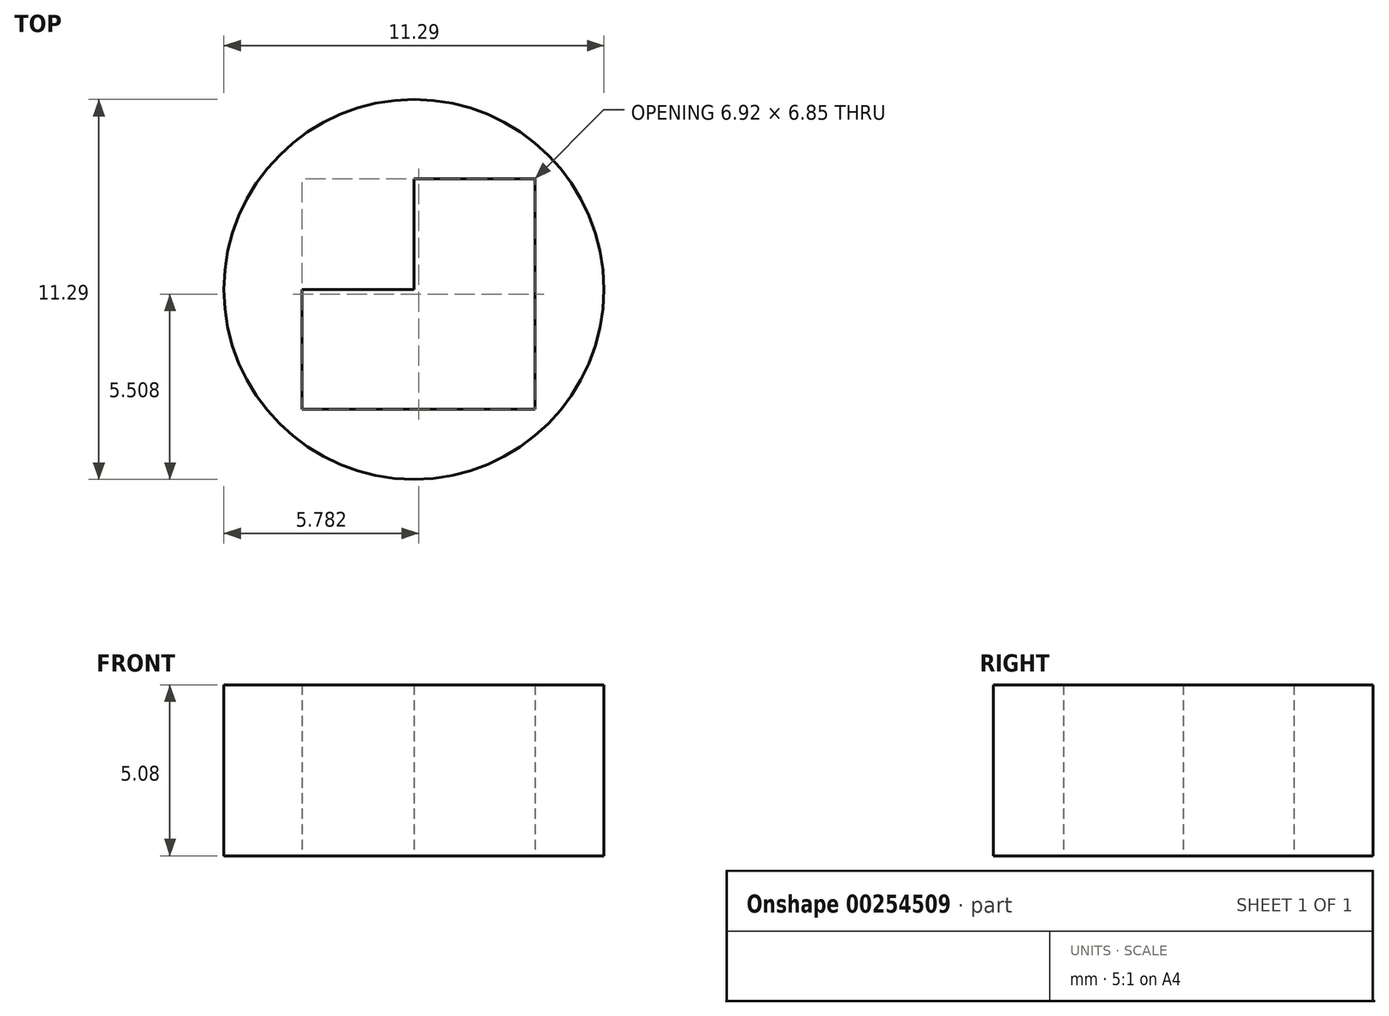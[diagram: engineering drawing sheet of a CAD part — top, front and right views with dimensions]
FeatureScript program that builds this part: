
annotation { "Feature Type Name" : "Feature", "Feature Type Description" : "" }
export const myFeature = defineFeature(function(context is Context, id is Id, definition is map)
    precondition{}
    {
        {
            var Q0;
            Q0=qCreatedBy(makeId("Top.planeOp"),FACE);
            var sketch = newSketch(context, id + "F0", { "sketchPlane" : qUnion([Q0])});
            skLineSegment(sketch, "E0", {"start": v(-33.45, 9.2) * mm, "end": v(-26.8, 16.12) * mm});
            skLineSegment(sketch, "E1", {"start": v(-26.8, 16.12) * mm, "end": v(-22.17, 16.12) * mm});
            skLineSegment(sketch, "E2", {"start": v(-22.17, 16.12) * mm, "end": v(-22.17, 19.99) * mm});
            skLineSegment(sketch, "E3", {"start": v(-22.17, 19.99) * mm, "end": v(-25.8, 19.97) * mm});
            skLineSegment(sketch, "E4", {"start": v(-25.8, 19.97) * mm, "end": v(-25.8, 38.73) * mm});
            skLineSegment(sketch, "E5", {"start": v(-25.8, 38.73) * mm, "end": v(-18.88, 45.9) * mm});
            skLineSegment(sketch, "E6", {"start": v(-18.88, 45.9) * mm, "end": v(14.3, 45.9) * mm});
            skLineSegment(sketch, "E7", {"start": v(14.3, 45.9) * mm, "end": v(22.2, 38.73) * mm});
            skLineSegment(sketch, "E8", {"start": v(22.2, 38.73) * mm, "end": v(22.2, 19.97) * mm});
            skLineSegment(sketch, "E9", {"start": v(22.2, 19.97) * mm, "end": v(18.52, 19.97) * mm});
            skLineSegment(sketch, "E10", {"start": v(18.52, 19.97) * mm, "end": v(18.52, 16.12) * mm});
            skLineSegment(sketch, "E11", {"start": v(18.52, 16.12) * mm, "end": v(22.2, 16.12) * mm});
            skLineSegment(sketch, "E12", {"start": v(22.2, 16.12) * mm, "end": v(29.83, 9.43) * mm});
            skLineSegment(sketch, "E13", {"start": v(29.83, 9.43) * mm, "end": v(29.83, -20.85) * mm});
            skLineSegment(sketch, "E14", {"start": v(29.83, -20.85) * mm, "end": v(22.14, -20.85) * mm});
            skLineSegment(sketch, "E15", {"start": v(22.14, -20.85) * mm, "end": v(22.14, -32.04) * mm});
            skLineSegment(sketch, "E16", {"start": v(22.14, -32.04) * mm, "end": v(19.03, -35.7) * mm});
            skLineSegment(sketch, "E17", {"start": v(19.03, -35.7) * mm, "end": v(3.87, -35.7) * mm});
            skLineSegment(sketch, "E18", {"start": v(3.87, -35.7) * mm, "end": v(3.87, -28.47) * mm});
            skLineSegment(sketch, "E19", {"start": v(3.87, -28.47) * mm, "end": v(-7.29, -28.47) * mm});
            skLineSegment(sketch, "E20", {"start": v(-7.29, -28.47) * mm, "end": v(-7.29, -35.7) * mm});
            skLineSegment(sketch, "E21", {"start": v(-7.29, -35.7) * mm, "end": v(-23.05, -35.7) * mm});
            skLineSegment(sketch, "E22", {"start": v(-23.05, -35.7) * mm, "end": v(-25.8, -32.44) * mm});
            skLineSegment(sketch, "E23", {"start": v(-25.8, -32.44) * mm, "end": v(-25.8, -20.85) * mm});
            skLineSegment(sketch, "E24", {"start": v(-25.8, -20.85) * mm, "end": v(-33.32, -20.85) * mm});
            skLineSegment(sketch, "E25", {"start": v(-33.32, -20.85) * mm, "end": v(-33.45, 9.2) * mm});
            skCircle(sketch, "E26", {"center": v(-11.3, 31.23) * mm, "radius": 5.9 * mm});
            skPoint(sketch, "E26.first.point", {"position": v(-17.19, 30.94) * mm});
            skPoint(sketch, "E26.second.point", {"position": v(-5.4, 31.07) * mm});
            skPoint(sketch, "E26.third.point", {"position": v(-11.26, 25.33) * mm});
            skCircle(sketch, "E27", {"center": v(7.12, 31) * mm, "radius": 5.64 * mm});
            skPoint(sketch, "E27.first.point", {"position": v(1.48, 30.84) * mm});
            skPoint(sketch, "E27.second.point", {"position": v(12.76, 30.78) * mm});
            skPoint(sketch, "E27.third.point", {"position": v(7.1, 36.64) * mm});
            skLineSegment(sketch, "E28.bottom", {"start": v(-14.96, 34.57) * mm, "end": v(-7.5, 34.57) * mm});
            skLineSegment(sketch, "E28.top", {"start": v(-14.96, 27.44) * mm, "end": v(-7.5, 27.44) * mm});
            skLineSegment(sketch, "E28.left", {"start": v(-14.96, 34.57) * mm, "end": v(-14.96, 27.44) * mm});
            skLineSegment(sketch, "E28.right", {"start": v(-7.5, 34.57) * mm, "end": v(-7.5, 27.44) * mm});
            skLineSegment(sketch, "E29.bottom", {"start": v(3.8, 34.28) * mm, "end": v(10.72, 34.28) * mm});
            skLineSegment(sketch, "E29.top", {"start": v(3.8, 27.44) * mm, "end": v(10.72, 27.44) * mm});
            skLineSegment(sketch, "E29.left", {"start": v(3.8, 34.28) * mm, "end": v(3.8, 27.44) * mm});
            skLineSegment(sketch, "E29.right", {"start": v(10.72, 34.28) * mm, "end": v(10.72, 27.44) * mm});
            skLineSegment(sketch, "E30.bottom", {"start": v(7.12, 31) * mm, "end": v(3.8, 31) * mm});
            skLineSegment(sketch, "E30.top", {"start": v(7.12, 34.28) * mm, "end": v(3.8, 34.28) * mm});
            skLineSegment(sketch, "E30.left", {"start": v(7.12, 31) * mm, "end": v(7.12, 34.28) * mm});
            skLineSegment(sketch, "E30.right", {"start": v(3.8, 31) * mm, "end": v(3.8, 34.28) * mm});
            skLineSegment(sketch, "E31.bottom", {"start": v(-11.3, 31.23) * mm, "end": v(-14.96, 31.23) * mm});
            skLineSegment(sketch, "E31.top", {"start": v(-11.3, 34.57) * mm, "end": v(-14.96, 34.57) * mm});
            skLineSegment(sketch, "E31.left", {"start": v(-11.3, 31.23) * mm, "end": v(-11.3, 34.57) * mm});
            skLineSegment(sketch, "E31.right", {"start": v(-14.96, 31.23) * mm, "end": v(-14.96, 34.57) * mm});
            skLineSegment(sketch, "E32.bottom", {"start": v(-3.8, 23.6) * mm, "end": v(0, 23.6) * mm});
            skLineSegment(sketch, "E32.top", {"start": v(-3.8, 19.8) * mm, "end": v(0, 19.8) * mm});
            skLineSegment(sketch, "E32.left", {"start": v(-3.8, 23.6) * mm, "end": v(-3.8, 19.8) * mm});
            skLineSegment(sketch, "E32.right", {"start": v(0, 23.6) * mm, "end": v(0, 19.8) * mm});
            skLineSegment(sketch, "E33.bottom", {"start": v(-7.5, 15.86) * mm, "end": v(3.8, 15.86) * mm});
            skLineSegment(sketch, "E33.top", {"start": v(-7.5, 12.27) * mm, "end": v(3.8, 12.27) * mm});
            skLineSegment(sketch, "E33.left", {"start": v(-7.5, 15.86) * mm, "end": v(-7.5, 12.27) * mm});
            skLineSegment(sketch, "E33.right", {"start": v(3.8, 15.86) * mm, "end": v(3.8, 12.27) * mm});
            skPoint(sketch, "E34.oppositeSnap0", {"position": v(-25.8, -26.64) * mm});
            skLineSegment(sketch, "E34.bottom", {"start": v(-29.45, -9.9) * mm, "end": v(-25.8, -9.9) * mm});
            skLineSegment(sketch, "E34.top", {"start": v(-29.45, -17.27) * mm, "end": v(-25.8, -17.27) * mm});
            skLineSegment(sketch, "E34.left", {"start": v(-29.45, -9.9) * mm, "end": v(-29.45, -17.27) * mm});
            skLineSegment(sketch, "E34.right", {"start": v(-25.8, -9.9) * mm, "end": v(-25.8, -17.27) * mm});
            skLineSegment(sketch, "E35.top", {"start": v(-29.45, 8.74) * mm, "end": v(-25.8, 8.74) * mm});
            skLineSegment(sketch, "E35.left", {"start": v(-29.45, -9.9) * mm, "end": v(-29.45, 8.74) * mm});
            skLineSegment(sketch, "E35.right", {"start": v(-25.8, -9.9) * mm, "end": v(-25.8, 8.74) * mm});
            skLineSegment(sketch, "E36.bottom", {"start": v(22.2, -9.9) * mm, "end": v(25.76, -9.9) * mm});
            skLineSegment(sketch, "E36.top", {"start": v(22.2, -17.27) * mm, "end": v(25.76, -17.27) * mm});
            skLineSegment(sketch, "E36.left", {"start": v(22.2, -9.9) * mm, "end": v(22.2, -17.27) * mm});
            skLineSegment(sketch, "E36.right", {"start": v(25.76, -9.9) * mm, "end": v(25.76, -17.27) * mm});
            skLineSegment(sketch, "E37.top", {"start": v(22.2, 8.7) * mm, "end": v(25.76, 8.7) * mm});
            skLineSegment(sketch, "E37.left", {"start": v(22.2, -9.9) * mm, "end": v(22.2, 8.7) * mm});
            skLineSegment(sketch, "E37.right", {"start": v(25.76, -9.9) * mm, "end": v(25.76, 8.7) * mm});
            skLineSegment(sketch, "E38.bottom", {"start": v(-3.6, -28.47) * mm, "end": v(0, -28.47) * mm});
            skLineSegment(sketch, "E38.top", {"start": v(-3.6, -24.74) * mm, "end": v(0, -24.74) * mm});
            skLineSegment(sketch, "E38.left", {"start": v(-3.6, -28.47) * mm, "end": v(-3.6, -24.74) * mm});
            skLineSegment(sketch, "E38.right", {"start": v(0, -28.47) * mm, "end": v(0, -24.74) * mm});
            skLineSegment(sketch, "E39", {"start": v(-22.24, -24.61) * mm, "end": v(-22.24, -31.85) * mm});
            skLineSegment(sketch, "E40", {"start": v(-22.24, -31.85) * mm, "end": v(-11.06, -31.85) * mm});
            skLineSegment(sketch, "E41", {"start": v(-11.06, -31.85) * mm, "end": v(-11.06, -28.48) * mm});
            skLineSegment(sketch, "E42", {"start": v(-11.06, -28.48) * mm, "end": v(-7.29, -28.47) * mm});
            skLineSegment(sketch, "E43", {"start": v(-7.29, -24.61) * mm, "end": v(-22.24, -24.61) * mm});
            skLineSegment(sketch, "E44", {"start": v(-7.29, -24.61) * mm, "end": v(-7.29, -28.47) * mm});
            skLineSegment(sketch, "E45", {"start": v(3.87, -28.47) * mm, "end": v(3.87, -24.61) * mm});
            skLineSegment(sketch, "E46", {"start": v(3.87, -24.61) * mm, "end": v(18.56, -24.61) * mm});
            skLineSegment(sketch, "E47", {"start": v(18.56, -24.61) * mm, "end": v(18.56, -31.97) * mm});
            skLineSegment(sketch, "E48", {"start": v(18.56, -31.97) * mm, "end": v(7.4, -31.97) * mm});
            skLineSegment(sketch, "E49", {"start": v(7.4, -31.97) * mm, "end": v(7.4, -28.47) * mm});
            skLineSegment(sketch, "E50", {"start": v(7.4, -28.47) * mm, "end": v(3.87, -28.47) * mm});
            skLineSegment(sketch, "E51", {"start": v(-22.17, 19.99) * mm, "end": v(-22.24, 38.23) * mm});
            skLineSegment(sketch, "E52", {"start": v(-22.24, 38.23) * mm, "end": v(-18.48, 38.25) * mm});
            skLineSegment(sketch, "E53", {"start": v(-18.48, 38.25) * mm, "end": v(-18.5, 42.04) * mm});
            skLineSegment(sketch, "E54", {"start": v(-18.5, 42.04) * mm, "end": v(14.76, 42.16) * mm});
            skLineSegment(sketch, "E55", {"start": v(14.76, 42.16) * mm, "end": v(14.78, 38.23) * mm});
            skLineSegment(sketch, "E56", {"start": v(14.78, 38.23) * mm, "end": v(18.52, 38.24) * mm});
            skLineSegment(sketch, "E57", {"start": v(18.52, 38.24) * mm, "end": v(18.52, 19.97) * mm});
            skLineSegment(sketch, "E58", {"start": v(3.8, 15.86) * mm, "end": v(3.8, 19.97) * mm});
            skLineSegment(sketch, "E59", {"start": v(3.8, 19.97) * mm, "end": v(18.52, 19.97) * mm});
            skLineSegment(sketch, "E60", {"start": v(-7.5, 15.86) * mm, "end": v(-7.5, 19.99) * mm});
            skLineSegment(sketch, "E61", {"start": v(-7.5, 19.99) * mm, "end": v(-22.17, 19.99) * mm});
            skLineSegment(sketch, "E62", {"start": v(-22.23, 12.38) * mm, "end": v(-22.23, -21.38) * mm});
            skLineSegment(sketch, "E63", {"start": v(-22.23, -21.38) * mm, "end": v(18.48, -21.38) * mm});
            skLineSegment(sketch, "E64", {"start": v(18.48, -21.38) * mm, "end": v(18.48, 12.34) * mm});
            skLineSegment(sketch, "E65", {"start": v(18.48, 12.34) * mm, "end": v(14.65, 12.34) * mm});
            skLineSegment(sketch, "E66", {"start": v(14.65, 12.34) * mm, "end": v(14.65, 15.86) * mm});
            skLineSegment(sketch, "E67", {"start": v(14.65, 15.86) * mm, "end": v(3.8, 15.86) * mm});
            skLineSegment(sketch, "E68", {"start": v(-22.23, 12.38) * mm, "end": v(-18.53, 12.38) * mm});
            skLineSegment(sketch, "E69", {"start": v(-18.53, 12.38) * mm, "end": v(-18.53, 15.86) * mm});
            skLineSegment(sketch, "E70", {"start": v(-18.53, 15.86) * mm, "end": v(-7.5, 15.86) * mm});
            skLineSegment(sketch, "E71.bottom", {"start": v(-7.42, -28.31) * mm, "end": v(-7.13, -28.31) * mm});
            skLineSegment(sketch, "E71.top", {"start": v(-7.42, -28.63) * mm, "end": v(-7.13, -28.63) * mm});
            skLineSegment(sketch, "E71.left", {"start": v(-7.42, -28.31) * mm, "end": v(-7.42, -28.63) * mm});
            skLineSegment(sketch, "E71.right", {"start": v(-7.13, -28.31) * mm, "end": v(-7.13, -28.63) * mm});
            skLineSegment(sketch, "E72.bottom", {"start": v(3.95, -28.38) * mm, "end": v(3.78, -28.38) * mm});
            skLineSegment(sketch, "E72.top", {"start": v(3.95, -28.56) * mm, "end": v(3.78, -28.56) * mm});
            skLineSegment(sketch, "E72.left", {"start": v(3.95, -28.38) * mm, "end": v(3.95, -28.56) * mm});
            skLineSegment(sketch, "E72.right", {"start": v(3.78, -28.38) * mm, "end": v(3.78, -28.56) * mm});
            skSolve(sketch);
        }
        {
            var Q0;
            Q0=makeQuery(id+"F0.imprint","IMPRINT",FACE,{"disambiguationData":[TD([[makeQuery(id+"F0.imprint","IMPRINT",EDGE,{"derivedFrom":sQuery(id+"F0.wireOp",EDGE,"E30.bottom")}),-1.0]])]});
            var Q1;
            Q1=makeQuery(id+"F0.imprint","IMPRINT",FACE,{"disambiguationData":[TD([[makeQuery(id+"F0.imprint","IMPRINT",EDGE,{"derivedFrom":sQuery(id+"F0.wireOp",EDGE,"E29.bottom")}),-1.0]])]});
            var Q2;
            Q2=makeQuery(id+"F0.imprint","IMPRINT",FACE,{"disambiguationData":[TD([[makeQuery(id+"F0.imprint","IMPRINT",EDGE,{"derivedFrom":sQuery(id+"F0.wireOp",EDGE,"E27")}),1.0]])]});
            extrude(context, id + "F1", {"entities" : qUnion([Q0, Q1, Q2]), "depth" : 5.08 * mm});
        }
    });
